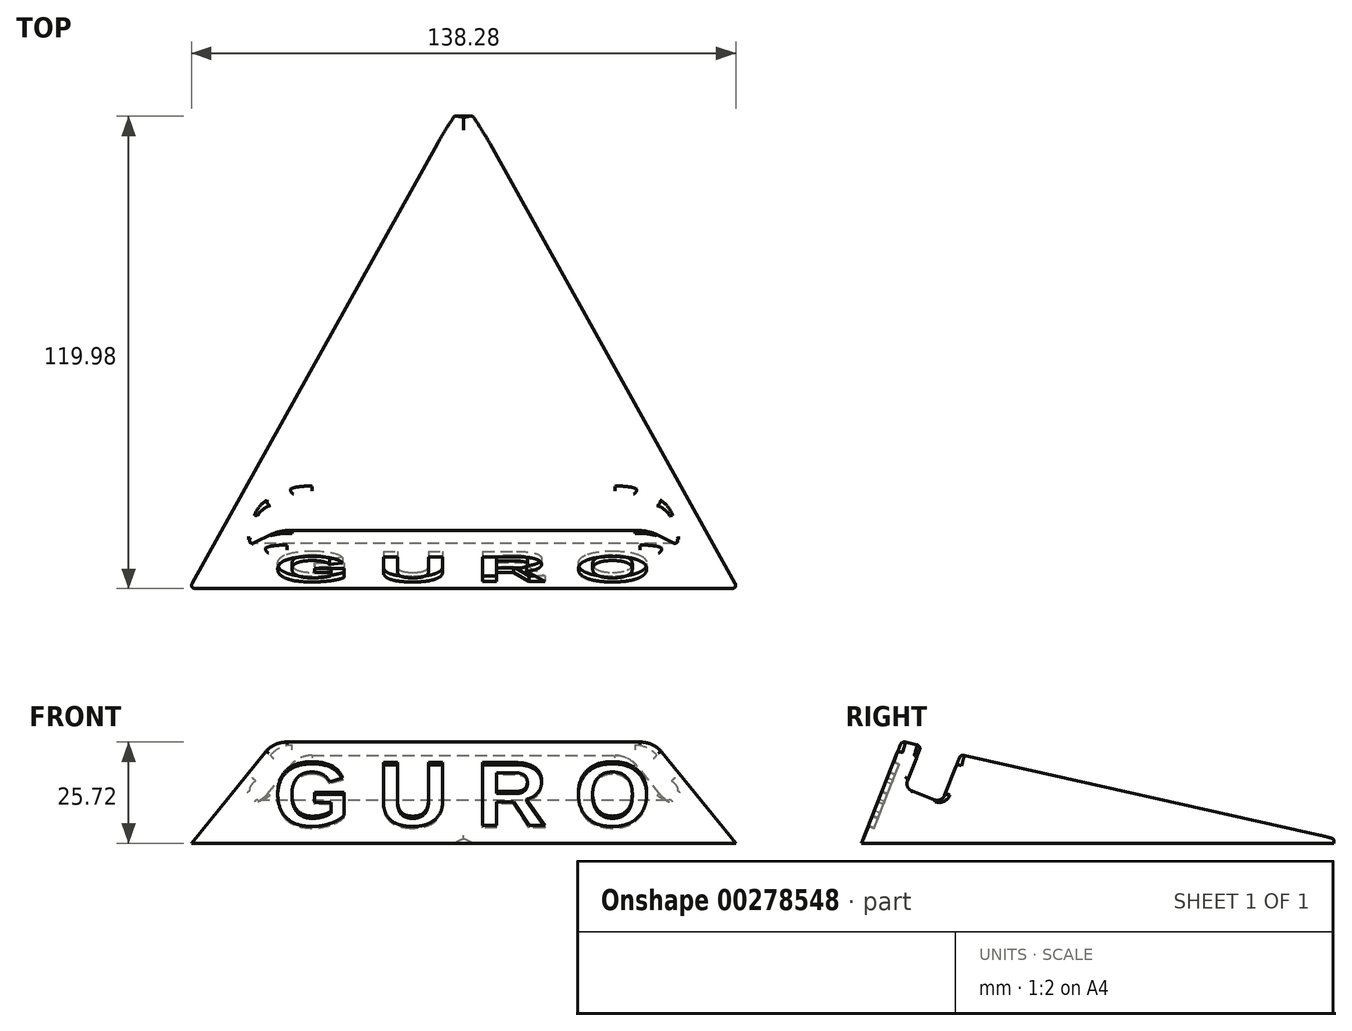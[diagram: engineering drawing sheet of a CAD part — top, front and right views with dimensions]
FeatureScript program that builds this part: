
annotation { "Feature Type Name" : "Feature", "Feature Type Description" : "" }
export const myFeature = defineFeature(function(context is Context, id is Id, definition is map)
    precondition{}
    {
        {
            var Q0;
            Q0=qCreatedBy(makeId("Top.planeOp"),FACE);
            var sketch = newSketch(context, id + "F0", { "sketchPlane" : qUnion([Q0])});
            skPoint(sketch, "E0.middle", {"position": v(0, 0) * mm});
            skLineSegment(sketch, "E1", {"start": v(0, 72.46) * mm, "end": v(0, -47.54) * mm});
            skLineSegment(sketch, "E2", {"start": v(0, -47.54) * mm, "end": v(-70, -47.54) * mm});
            skLineSegment(sketch, "E3", {"start": v(-70, -47.54) * mm, "end": v(-19, 72.46) * mm});
            skLineSegment(sketch, "E4", {"start": v(-19, 72.46) * mm, "end": v(0, 72.46) * mm});
            skLineSegment(sketch, "E5.MirrorCS", {"start": v(19, 72.46) * mm, "end": v(0, 72.46) * mm});
            skLineSegment(sketch, "E6.MirrorCS", {"start": v(70, -47.54) * mm, "end": v(19, 72.46) * mm});
            skLineSegment(sketch, "E7.MirrorCS", {"start": v(0, -47.54) * mm, "end": v(70, -47.54) * mm});
            skSolve(sketch);
        }
        {
            var Q0;
            Q0=makeQuery(id+"F0.imprint","IMPRINT",FACE,{"disambiguationData":[TD([[makeQuery(id+"F0.imprint","IMPRINT",EDGE,{"derivedFrom":sQuery(id+"F0.wireOp",EDGE,"E1")}),-1.0]])]});
            var Q1;
            Q1=makeQuery(id+"F0.imprint","IMPRINT",FACE,{"disambiguationData":[TD([[makeQuery(id+"F0.imprint","IMPRINT",EDGE,{"derivedFrom":sQuery(id+"F0.wireOp",EDGE,"E1")}),1.0]])]});
            extrude(context, id + "F1", {"entities" : qUnion([Q0, Q1]), "depth" : 28 * mm});
        }
        {
            var Q0;
            Q0=qCreatedBy(makeId("Right.planeOp"),FACE);
            var sketch = newSketch(context, id + "F2", { "sketchPlane" : qUnion([Q0])});
            skLineSegment(sketch, "E8", {"start": v(-47.52, 0) * mm, "end": v(-37.37, 25.88) * mm});
            skLineSegment(sketch, "E9", {"start": v(-37.37, 25.88) * mm, "end": v(-32.4, 24.77) * mm});
            skLineSegment(sketch, "E10", {"start": v(73.21, 1.08) * mm, "end": v(73.21, 32.39) * mm});
            skLineSegment(sketch, "E11", {"start": v(73.21, 32.39) * mm, "end": v(-55.5, 31.08) * mm});
            skLineSegment(sketch, "E12", {"start": v(-55.5, 31.08) * mm, "end": v(-55.5, 0) * mm});
            skLineSegment(sketch, "E13", {"start": v(-55.5, 0) * mm, "end": v(-47.52, 0) * mm});
            skLineSegment(sketch, "E14", {"start": v(-32.4, 24.77) * mm, "end": v(-36.62, 14) * mm});
            skLineSegment(sketch, "E15", {"start": v(-36.62, 14) * mm, "end": v(-27.18, 10.3) * mm});
            skLineSegment(sketch, "E16", {"start": v(-27.18, 10.3) * mm, "end": v(-22.38, 22.52) * mm});
            skLineSegment(sketch, "E17.trimOffspring", {"start": v(-22.38, 22.52) * mm, "end": v(73.21, 1.08) * mm});
            skSolve(sketch);
        }
        {
            var Q0;
            Q0 = qSketchRegion(id + "F2", true);
            extrude(context, id + "F3", {"entities" : qUnion([Q0]), "operationType" : NewBodyOperationType.REMOVE, "endBound" : BoundingType.SYMMETRIC, "oppositeDirection" : true, "depth" : 160 * mm});
        }
        {
            var Q0;
            Q0=makeQuery(id+"F3.boolean.opBoolean","INTERSECT",EDGE,{"derivedFrom":[makeQuery(id+"F1.opExtrude","SWEPT_FACE",FACE,{"disambiguationData":[OSD([sQuery(id+"F0.wireOp",EDGE,"E6.MirrorCS")])]}),makeQuery(id+"F3.opExtrude","SWEPT_FACE",FACE,{"disambiguationData":[OSD([sQuery(id+"F2.wireOp",EDGE,"E17.trimOffspring")])]})]});
            var Q1;
            Q1=makeQuery(id+"F3.boolean.opBoolean","INTERSECT",EDGE,{"derivedFrom":[makeQuery(id+"F1.opExtrude","SWEPT_FACE",FACE,{"disambiguationData":[OSD([sQuery(id+"F0.wireOp",EDGE,"E3")])]}),makeQuery(id+"F3.opExtrude","SWEPT_FACE",FACE,{"disambiguationData":[OSD([sQuery(id+"F2.wireOp",EDGE,"E17.trimOffspring")])]})]});
            chamfer(context, id + "F4", {"entities" : qUnion([Q0, Q1]), "chamferType" : ChamferType.OFFSET_ANGLE, "width" : 28 * mm, "oppositeDirection" : false, "angle" : 28 * degree, "tangentPropagation" : true});
        }
        {
            var Q0;
            Q0=makeQuery(id+"F3.boolean.opBoolean","COPY",FACE,{"derivedFrom":makeQuery(id+"F3.opExtrude","SWEPT_FACE",FACE,{"disambiguationData":[OSD([sQuery(id+"F2.wireOp",EDGE,"E8")])]})});
            var sketch = newSketch(context, id + "F5", { "sketchPlane" : qUnion([Q0])});
            skText(sketch, "E18", { "text": "G U R O", "fontName": "Arimo-Bold.ttf"});
            const initialGuessF5  = {"E18": [-0.04826, -0.01256, 1, 0, 0.018]};
            skSetInitialGuess(sketch, initialGuessF5);
            skSolve(sketch);
        }
        {
            var Q0;
            Q0=makeQuery(id+"F5.imprint","IMPRINT",FACE,{"disambiguationData":[TD([[makeQuery(id+"F5.imprint","IMPRINT",EDGE,{"derivedFrom":sQuery(id+"F5.wireOp",EDGE,"E18.sketch_text.stroke-0")}),-1.0]])]});
            var Q1;
            Q1=makeQuery(id+"F5.imprint","IMPRINT",FACE,{"disambiguationData":[TD([[makeQuery(id+"F5.imprint","IMPRINT",EDGE,{"derivedFrom":sQuery(id+"F5.wireOp",EDGE,"E18.sketch_text.stroke-21")}),-1.0]])]});
            var Q2;
            Q2=makeQuery(id+"F5.imprint","IMPRINT",FACE,{"disambiguationData":[TD([[makeQuery(id+"F5.imprint","IMPRINT",EDGE,{"derivedFrom":sQuery(id+"F5.wireOp",EDGE,"E18.sketch_text.stroke-35")}),-1.0]])]});
            var Q3;
            Q3=makeQuery(id+"F5.imprint","IMPRINT",FACE,{"disambiguationData":[TD([[makeQuery(id+"F5.imprint","IMPRINT",EDGE,{"derivedFrom":sQuery(id+"F5.wireOp",EDGE,"E18.sketch_text.stroke-53")}),-1.0]])]});
            extrude(context, id + "F6", {"entities" : qUnion([Q0, Q1, Q2, Q3]), "operationType" : NewBodyOperationType.REMOVE, "oppositeDirection" : true, "depth" : 1.5 * mm});
        }
        {
            var Q0;
            Q0=makeQuery(id+"F3.boolean.opBoolean","COPY",EDGE,{"derivedFrom":makeQuery(id+"F3.opExtrude","SWEPT_EDGE",EDGE,{"disambiguationData":[OSD([sQuery(id+"F2.wireOp",EDGE,"E14"),sQuery(id+"F2.wireOp",EDGE,"E15")])]})});
            var Q1;
            Q1=makeQuery(id+"F3.boolean.opBoolean","COPY",EDGE,{"derivedFrom":makeQuery(id+"F3.opExtrude","SWEPT_EDGE",EDGE,{"disambiguationData":[OSD([sQuery(id+"F2.wireOp",EDGE,"E15"),sQuery(id+"F2.wireOp",EDGE,"E16")])]})});
            fillet(context, id + "F7", {"entities" : qUnion([Q0, Q1]), "radius" : 2 * mm, "tangentPropagation" : true, "allowEdgeOverflow" : false});
        }
        {
            var Q0;
            Q0=makeQuery(id+"F4.opChamfer","BLEND_EDGE",EDGE,{"blendedFrom":[makeQuery(id+"F3.boolean.opBoolean","INTERSECT",EDGE,{"derivedFrom":[makeQuery(id+"F1.opExtrude","SWEPT_FACE",FACE,{"disambiguationData":[OSD([sQuery(id+"F0.wireOp",EDGE,"E6.MirrorCS")])]}),makeQuery(id+"F3.opExtrude","SWEPT_FACE",FACE,{"disambiguationData":[OSD([sQuery(id+"F2.wireOp",EDGE,"E17.trimOffspring")])]})]}),makeQuery(id+"F3.boolean.opBoolean","COPY",FACE,{"derivedFrom":makeQuery(id+"F3.opExtrude","SWEPT_FACE",FACE,{"disambiguationData":[OSD([sQuery(id+"F2.wireOp",EDGE,"E16")])]})})],"blendedInto":[makeQuery(id+"F3.boolean.opBoolean","COPY",FACE,{"derivedFrom":makeQuery(id+"F3.opExtrude","SWEPT_FACE",FACE,{"disambiguationData":[OSD([sQuery(id+"F2.wireOp",EDGE,"E16")])]})})]});
            var Q1;
            Q1=makeQuery(id+"F7.opFillet","BLEND_EDGE",EDGE,{"blendedFrom":[makeQuery(id+"F3.boolean.opBoolean","COPY",EDGE,{"derivedFrom":makeQuery(id+"F3.opExtrude","SWEPT_EDGE",EDGE,{"disambiguationData":[OSD([sQuery(id+"F2.wireOp",EDGE,"E15"),sQuery(id+"F2.wireOp",EDGE,"E16")])]})}),makeQuery(id+"F4.opChamfer","BLEND_FACE",FACE,{"disambiguationData":[OSD([sQuery(id+"F0.wireOp",EDGE,"E6.MirrorCS"),sQuery(id+"F2.wireOp",EDGE,"E17.trimOffspring")])]})],"blendedInto":[makeQuery(id+"F4.opChamfer","BLEND_FACE",FACE,{"disambiguationData":[OSD([sQuery(id+"F0.wireOp",EDGE,"E6.MirrorCS"),sQuery(id+"F2.wireOp",EDGE,"E17.trimOffspring")])]})]});
            var Q2;
            Q2=makeQuery(id+"F4.opChamfer","BLEND_EDGE",EDGE,{"blendedFrom":[makeQuery(id+"F3.boolean.opBoolean","INTERSECT",EDGE,{"derivedFrom":[makeQuery(id+"F1.opExtrude","SWEPT_FACE",FACE,{"disambiguationData":[OSD([sQuery(id+"F0.wireOp",EDGE,"E6.MirrorCS")])]}),makeQuery(id+"F3.opExtrude","SWEPT_FACE",FACE,{"disambiguationData":[OSD([sQuery(id+"F2.wireOp",EDGE,"E17.trimOffspring")])]})]}),makeQuery(id+"F3.boolean.opBoolean","COPY",FACE,{"derivedFrom":makeQuery(id+"F3.opExtrude","SWEPT_FACE",FACE,{"disambiguationData":[OSD([sQuery(id+"F2.wireOp",EDGE,"E15")])]})})],"blendedInto":[makeQuery(id+"F3.boolean.opBoolean","COPY",FACE,{"derivedFrom":makeQuery(id+"F3.opExtrude","SWEPT_FACE",FACE,{"disambiguationData":[OSD([sQuery(id+"F2.wireOp",EDGE,"E15")])]})})]});
            var Q3;
            Q3=makeQuery(id+"F7.opFillet","BLEND_EDGE",EDGE,{"blendedFrom":[makeQuery(id+"F3.boolean.opBoolean","COPY",EDGE,{"derivedFrom":makeQuery(id+"F3.opExtrude","SWEPT_EDGE",EDGE,{"disambiguationData":[OSD([sQuery(id+"F2.wireOp",EDGE,"E14"),sQuery(id+"F2.wireOp",EDGE,"E15")])]})}),makeQuery(id+"F4.opChamfer","BLEND_FACE",FACE,{"disambiguationData":[OSD([sQuery(id+"F0.wireOp",EDGE,"E6.MirrorCS"),sQuery(id+"F2.wireOp",EDGE,"E17.trimOffspring")])]})],"blendedInto":[makeQuery(id+"F4.opChamfer","BLEND_FACE",FACE,{"disambiguationData":[OSD([sQuery(id+"F0.wireOp",EDGE,"E6.MirrorCS"),sQuery(id+"F2.wireOp",EDGE,"E17.trimOffspring")])]})]});
            var Q4;
            Q4=makeQuery(id+"F4.opChamfer","BLEND_EDGE",EDGE,{"blendedFrom":[makeQuery(id+"F3.boolean.opBoolean","INTERSECT",EDGE,{"derivedFrom":[makeQuery(id+"F1.opExtrude","SWEPT_FACE",FACE,{"disambiguationData":[OSD([sQuery(id+"F0.wireOp",EDGE,"E6.MirrorCS")])]}),makeQuery(id+"F3.opExtrude","SWEPT_FACE",FACE,{"disambiguationData":[OSD([sQuery(id+"F2.wireOp",EDGE,"E17.trimOffspring")])]})]}),makeQuery(id+"F3.boolean.opBoolean","COPY",FACE,{"derivedFrom":makeQuery(id+"F3.opExtrude","SWEPT_FACE",FACE,{"disambiguationData":[OSD([sQuery(id+"F2.wireOp",EDGE,"E14")])]})})],"blendedInto":[makeQuery(id+"F3.boolean.opBoolean","COPY",FACE,{"derivedFrom":makeQuery(id+"F3.opExtrude","SWEPT_FACE",FACE,{"disambiguationData":[OSD([sQuery(id+"F2.wireOp",EDGE,"E14")])]})})]});
            var Q5;
            Q5=makeQuery(id+"F4.opChamfer","BLEND_EDGE",EDGE,{"blendedFrom":[makeQuery(id+"F3.boolean.opBoolean","INTERSECT",EDGE,{"derivedFrom":[makeQuery(id+"F1.opExtrude","SWEPT_FACE",FACE,{"disambiguationData":[OSD([sQuery(id+"F0.wireOp",EDGE,"E6.MirrorCS")])]}),makeQuery(id+"F3.opExtrude","SWEPT_FACE",FACE,{"disambiguationData":[OSD([sQuery(id+"F2.wireOp",EDGE,"E17.trimOffspring")])]})]}),makeQuery(id+"F3.boolean.opBoolean","COPY",FACE,{"derivedFrom":makeQuery(id+"F3.opExtrude","SWEPT_FACE",FACE,{"disambiguationData":[OSD([sQuery(id+"F2.wireOp",EDGE,"E8")])]})})],"blendedInto":[makeQuery(id+"F3.boolean.opBoolean","COPY",FACE,{"derivedFrom":makeQuery(id+"F3.opExtrude","SWEPT_FACE",FACE,{"disambiguationData":[OSD([sQuery(id+"F2.wireOp",EDGE,"E8")])]})})]});
            var Q6;
            Q6=makeQuery(id+"F4.opChamfer","BLEND_EDGE",EDGE,{"blendedFrom":[makeQuery(id+"F3.boolean.opBoolean","INTERSECT",EDGE,{"derivedFrom":[makeQuery(id+"F1.opExtrude","SWEPT_FACE",FACE,{"disambiguationData":[OSD([sQuery(id+"F0.wireOp",EDGE,"E3")])]}),makeQuery(id+"F3.opExtrude","SWEPT_FACE",FACE,{"disambiguationData":[OSD([sQuery(id+"F2.wireOp",EDGE,"E17.trimOffspring")])]})]}),makeQuery(id+"F3.boolean.opBoolean","COPY",FACE,{"derivedFrom":makeQuery(id+"F3.opExtrude","SWEPT_FACE",FACE,{"disambiguationData":[OSD([sQuery(id+"F2.wireOp",EDGE,"E8")])]})})],"blendedInto":[makeQuery(id+"F3.boolean.opBoolean","COPY",FACE,{"derivedFrom":makeQuery(id+"F3.opExtrude","SWEPT_FACE",FACE,{"disambiguationData":[OSD([sQuery(id+"F2.wireOp",EDGE,"E8")])]})})]});
            var Q7;
            Q7=makeQuery(id+"F3.boolean.opBoolean","INTERSECT",EDGE,{"derivedFrom":[makeQuery(id+"F1.opExtrude","SWEPT_FACE",FACE,{"disambiguationData":[OSD([sQuery(id+"F0.wireOp",EDGE,"E4"),sQuery(id+"F0.wireOp",EDGE,"E5.MirrorCS")])]}),makeQuery(id+"F3.opExtrude","SWEPT_FACE",FACE,{"disambiguationData":[OSD([sQuery(id+"F2.wireOp",EDGE,"E17.trimOffspring")])]})]});
            var Q8;
            Q8=makeQuery(id+"F4.opChamfer","BLEND_EDGE",EDGE,{"blendedFrom":[makeQuery(id+"F3.boolean.opBoolean","INTERSECT",EDGE,{"derivedFrom":[makeQuery(id+"F1.opExtrude","SWEPT_FACE",FACE,{"disambiguationData":[OSD([sQuery(id+"F0.wireOp",EDGE,"E3")])]}),makeQuery(id+"F3.opExtrude","SWEPT_FACE",FACE,{"disambiguationData":[OSD([sQuery(id+"F2.wireOp",EDGE,"E17.trimOffspring")])]})]}),makeQuery(id+"F3.boolean.opBoolean","COPY",FACE,{"derivedFrom":makeQuery(id+"F3.opExtrude","SWEPT_FACE",FACE,{"disambiguationData":[OSD([sQuery(id+"F2.wireOp",EDGE,"E14")])]})})],"blendedInto":[makeQuery(id+"F3.boolean.opBoolean","COPY",FACE,{"derivedFrom":makeQuery(id+"F3.opExtrude","SWEPT_FACE",FACE,{"disambiguationData":[OSD([sQuery(id+"F2.wireOp",EDGE,"E14")])]})})]});
            var Q9;
            Q9=makeQuery(id+"F7.opFillet","BLEND_EDGE",EDGE,{"blendedFrom":[makeQuery(id+"F3.boolean.opBoolean","COPY",EDGE,{"derivedFrom":makeQuery(id+"F3.opExtrude","SWEPT_EDGE",EDGE,{"disambiguationData":[OSD([sQuery(id+"F2.wireOp",EDGE,"E14"),sQuery(id+"F2.wireOp",EDGE,"E15")])]})}),makeQuery(id+"F4.opChamfer","BLEND_FACE",FACE,{"disambiguationData":[OSD([sQuery(id+"F0.wireOp",EDGE,"E3"),sQuery(id+"F2.wireOp",EDGE,"E17.trimOffspring")])]})],"blendedInto":[makeQuery(id+"F4.opChamfer","BLEND_FACE",FACE,{"disambiguationData":[OSD([sQuery(id+"F0.wireOp",EDGE,"E3"),sQuery(id+"F2.wireOp",EDGE,"E17.trimOffspring")])]})]});
            var Q10;
            Q10=makeQuery(id+"F4.opChamfer","BLEND_EDGE",EDGE,{"blendedFrom":[makeQuery(id+"F3.boolean.opBoolean","INTERSECT",EDGE,{"derivedFrom":[makeQuery(id+"F1.opExtrude","SWEPT_FACE",FACE,{"disambiguationData":[OSD([sQuery(id+"F0.wireOp",EDGE,"E3")])]}),makeQuery(id+"F3.opExtrude","SWEPT_FACE",FACE,{"disambiguationData":[OSD([sQuery(id+"F2.wireOp",EDGE,"E17.trimOffspring")])]})]}),makeQuery(id+"F3.boolean.opBoolean","COPY",FACE,{"derivedFrom":makeQuery(id+"F3.opExtrude","SWEPT_FACE",FACE,{"disambiguationData":[OSD([sQuery(id+"F2.wireOp",EDGE,"E15")])]})})],"blendedInto":[makeQuery(id+"F3.boolean.opBoolean","COPY",FACE,{"derivedFrom":makeQuery(id+"F3.opExtrude","SWEPT_FACE",FACE,{"disambiguationData":[OSD([sQuery(id+"F2.wireOp",EDGE,"E15")])]})})]});
            var Q11;
            Q11=makeQuery(id+"F7.opFillet","BLEND_EDGE",EDGE,{"blendedFrom":[makeQuery(id+"F3.boolean.opBoolean","COPY",EDGE,{"derivedFrom":makeQuery(id+"F3.opExtrude","SWEPT_EDGE",EDGE,{"disambiguationData":[OSD([sQuery(id+"F2.wireOp",EDGE,"E15"),sQuery(id+"F2.wireOp",EDGE,"E16")])]})}),makeQuery(id+"F4.opChamfer","BLEND_FACE",FACE,{"disambiguationData":[OSD([sQuery(id+"F0.wireOp",EDGE,"E3"),sQuery(id+"F2.wireOp",EDGE,"E17.trimOffspring")])]})],"blendedInto":[makeQuery(id+"F4.opChamfer","BLEND_FACE",FACE,{"disambiguationData":[OSD([sQuery(id+"F0.wireOp",EDGE,"E3"),sQuery(id+"F2.wireOp",EDGE,"E17.trimOffspring")])]})]});
            var Q12;
            Q12=makeQuery(id+"F4.opChamfer","BLEND_EDGE",EDGE,{"blendedFrom":[makeQuery(id+"F3.boolean.opBoolean","INTERSECT",EDGE,{"derivedFrom":[makeQuery(id+"F1.opExtrude","SWEPT_FACE",FACE,{"disambiguationData":[OSD([sQuery(id+"F0.wireOp",EDGE,"E3")])]}),makeQuery(id+"F3.opExtrude","SWEPT_FACE",FACE,{"disambiguationData":[OSD([sQuery(id+"F2.wireOp",EDGE,"E17.trimOffspring")])]})]}),makeQuery(id+"F3.boolean.opBoolean","COPY",FACE,{"derivedFrom":makeQuery(id+"F3.opExtrude","SWEPT_FACE",FACE,{"disambiguationData":[OSD([sQuery(id+"F2.wireOp",EDGE,"E16")])]})})],"blendedInto":[makeQuery(id+"F3.boolean.opBoolean","COPY",FACE,{"derivedFrom":makeQuery(id+"F3.opExtrude","SWEPT_FACE",FACE,{"disambiguationData":[OSD([sQuery(id+"F2.wireOp",EDGE,"E16")])]})})]});
            var Q13;
            Q13=makeQuery(id+"F3.boolean.opBoolean","COPY",EDGE,{"derivedFrom":makeQuery(id+"F3.opExtrude","SWEPT_EDGE",EDGE,{"disambiguationData":[OSD([sQuery(id+"F2.wireOp",EDGE,"E16"),sQuery(id+"F2.wireOp",EDGE,"E17.trimOffspring")])]})});
            var Q14;
            Q14=makeQuery(id+"F3.boolean.opBoolean","COPY",EDGE,{"derivedFrom":makeQuery(id+"F3.opExtrude","SWEPT_EDGE",EDGE,{"disambiguationData":[OSD([sQuery(id+"F2.wireOp",EDGE,"E9"),sQuery(id+"F2.wireOp",EDGE,"E14")])]})});
            var Q15;
            Q15=makeQuery(id+"F3.boolean.opBoolean","COPY",EDGE,{"derivedFrom":makeQuery(id+"F3.opExtrude","SWEPT_EDGE",EDGE,{"disambiguationData":[OSD([sQuery(id+"F2.wireOp",EDGE,"E8"),sQuery(id+"F2.wireOp",EDGE,"E9")])]})});
            fillet(context, id + "F8", {"entities" : qUnion([Q0, Q1, Q2, Q3, Q4, Q5, Q6, Q7, Q8, Q9, Q10, Q11, Q12, Q13, Q14, Q15]), "radius" : 1 * mm, "tangentPropagation" : true, "allowEdgeOverflow" : false});
        }
        {
            var Q0;
            {var subQ0=makeQuery(id+"F3.opExtrude","SWEPT_FACE",FACE,{"disambiguationData":[OSD([sQuery(id+"F2.wireOp",EDGE,"E17.trimOffspring")])]});Q0=makeQuery(id+"F4.opChamfer","BLEND_EDGE",EDGE,{"blendedFrom":[makeQuery(id+"F3.boolean.opBoolean","INTERSECT",EDGE,{"derivedFrom":[makeQuery(id+"F1.opExtrude","SWEPT_FACE",FACE,{"disambiguationData":[OSD([sQuery(id+"F0.wireOp",EDGE,"E3")])]}),subQ0]}),makeQuery(id+"F3.boolean.opBoolean","COPY",FACE,{"derivedFrom":subQ0})],"blendedInto":[makeQuery(id+"F3.boolean.opBoolean","COPY",FACE,{"derivedFrom":subQ0})]});}
            var Q1;
            {var subQ0=makeQuery(id+"F3.opExtrude","SWEPT_FACE",FACE,{"disambiguationData":[OSD([sQuery(id+"F2.wireOp",EDGE,"E17.trimOffspring")])]});Q1=makeQuery(id+"F4.opChamfer","BLEND_EDGE",EDGE,{"blendedFrom":[makeQuery(id+"F3.boolean.opBoolean","INTERSECT",EDGE,{"derivedFrom":[makeQuery(id+"F1.opExtrude","SWEPT_FACE",FACE,{"disambiguationData":[OSD([sQuery(id+"F0.wireOp",EDGE,"E6.MirrorCS")])]}),subQ0]}),makeQuery(id+"F3.boolean.opBoolean","COPY",FACE,{"derivedFrom":subQ0})],"blendedInto":[makeQuery(id+"F3.boolean.opBoolean","COPY",FACE,{"derivedFrom":subQ0})]});}
            var Q2;
            Q2=makeQuery(id+"F4.opChamfer","BLEND_EDGE",EDGE,{"blendedFrom":[makeQuery(id+"F3.boolean.opBoolean","INTERSECT",EDGE,{"derivedFrom":[makeQuery(id+"F1.opExtrude","SWEPT_FACE",FACE,{"disambiguationData":[OSD([sQuery(id+"F0.wireOp",EDGE,"E3")])]}),makeQuery(id+"F3.opExtrude","SWEPT_FACE",FACE,{"disambiguationData":[OSD([sQuery(id+"F2.wireOp",EDGE,"E17.trimOffspring")])]})]}),makeQuery(id+"F3.boolean.opBoolean","COPY",FACE,{"derivedFrom":makeQuery(id+"F3.opExtrude","SWEPT_FACE",FACE,{"disambiguationData":[OSD([sQuery(id+"F2.wireOp",EDGE,"E9")])]})})],"blendedInto":[makeQuery(id+"F3.boolean.opBoolean","COPY",FACE,{"derivedFrom":makeQuery(id+"F3.opExtrude","SWEPT_FACE",FACE,{"disambiguationData":[OSD([sQuery(id+"F2.wireOp",EDGE,"E9")])]})})]});
            var Q3;
            Q3=makeQuery(id+"F4.opChamfer","BLEND_EDGE",EDGE,{"blendedFrom":[makeQuery(id+"F3.boolean.opBoolean","INTERSECT",EDGE,{"derivedFrom":[makeQuery(id+"F1.opExtrude","SWEPT_FACE",FACE,{"disambiguationData":[OSD([sQuery(id+"F0.wireOp",EDGE,"E6.MirrorCS")])]}),makeQuery(id+"F3.opExtrude","SWEPT_FACE",FACE,{"disambiguationData":[OSD([sQuery(id+"F2.wireOp",EDGE,"E17.trimOffspring")])]})]}),makeQuery(id+"F3.boolean.opBoolean","COPY",FACE,{"derivedFrom":makeQuery(id+"F3.opExtrude","SWEPT_FACE",FACE,{"disambiguationData":[OSD([sQuery(id+"F2.wireOp",EDGE,"E9")])]})})],"blendedInto":[makeQuery(id+"F3.boolean.opBoolean","COPY",FACE,{"derivedFrom":makeQuery(id+"F3.opExtrude","SWEPT_FACE",FACE,{"disambiguationData":[OSD([sQuery(id+"F2.wireOp",EDGE,"E9")])]})})]});
            fillet(context, id + "F9", {"entities" : qUnion([Q0, Q1, Q2, Q3]), "radius" : 6 * mm, "tangentPropagation" : true, "allowEdgeOverflow" : false});
        }
    });
